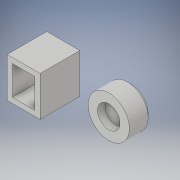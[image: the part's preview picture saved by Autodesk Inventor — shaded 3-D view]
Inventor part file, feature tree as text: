
AUTODESK INVENTOR PART (.ipt)
format: ipt  version: 2018 (Build 220112000, 112)  size: 135,680 bytes
history: native  units: in
note: dims shown in document units (in); Inventor stores cm internally (conversion verified against a paired STEP export)
features: extrude x4, sketch x4, chamfer x2, projected_geometry x1
ambient origin geometry x8: Origin, YZ Plane, XZ Plane, XY Plane, X Axis, Y Axis, Z Axis, Center Point
bodies: Solid1 (feature_tree)
feature tree (11):
  extrude  "Extrusion1"  Depth=0.1181in TaperAngle=0.0deg
  extrude  "Extrusion2"  Depth=0.0394in TaperAngle=0.0deg
  chamfer  "Chamfer1"  Distance=0.0197in Angle=45.0deg
  extrude  "Extrusion3"  Depth=0.1535in
  extrude  "Extrusion4"  Depth=0.2283in TaperAngle=0.0deg
  chamfer  "Chamfer2"  Distance=0.0787in
  sketch  "Sketch1"  dims[d0=0.2165in d1=0.1181in d2=0.0in]
  sketch  "Sketch2"  dims[d3=0.1181in d4=0.0394in d5=0.0in d6=0.0197in d7=0.125in d8=45.0deg]
  sketch  "Sketch3"  dims[d9=0.1181in d10=0.1535in]
  sketch  "Sketch4"  dims[d11=0.0276in d12=0.2283in d13=0.0in d14=0.0787in d15=0.0in d16=0.0197in d17=0.125in d18=45.0deg]
  projected_geometry  "Projected Loop1"
